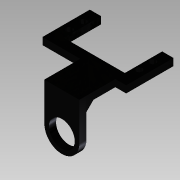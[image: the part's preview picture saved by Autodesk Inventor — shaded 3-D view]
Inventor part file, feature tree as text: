
AUTODESK INVENTOR PART (.ipt)
format: ipt  version: 2015 SP1 (Build 190203100, 203)  size: 286,208 bytes
history: native  units: mm
features: extrude x12, sketch x11, projected_geometry x4, plane x2, mirror x1
ambient origin geometry x8: Origin, YZ Plane, XZ Plane, XY Plane, X Axis, Y Axis, Z Axis, Center Point
bodies: Solid1 (feature_tree)
feature tree (30):
  sketch  "Sketch1"  dims[d19=3.0mm d20=0.0mm d22=39.4615mm]
  extrude  "Extrusion1"  Depth=39.4615mm
  plane  "Work Plane1"
  extrude  "Extrusion2"  Depth=24.75mm TaperAngle=0.0deg
  extrude  "Extrusion3"  Depth=24.75mm
  extrude  "Extrusion4"  Depth=4.980307mm
  extrude  "Extrusion5"  Depth=10.0mm TaperAngle=0.0deg
  extrude  "Extrusion6"  Depth=2.0mm
  extrude  "Extrusion7"  Depth=5.0mm TaperAngle=0.0deg
  extrude  "Extrusion8"  Depth=5.0mm TaperAngle=0.0deg
  extrude  "Extrusion9"  Depth=1.0mm
  mirror  "Mirror1"
  extrude  "Extrusion10"  TaperAngle=0.0deg  [1 undecoded]
  extrude  "Extrusion11"  Depth=5.0mm
  plane  "Work Plane2"
  sketch  "Sketch12"  dims[d64=7.0mm d65=6.460614mm d66=5.0mm d67=0.0mm d68=7.974mm d69=5.0mm d70=5.0mm d71=0.0mm d72=59.16mm d73=5.0mm d74=0.0mm d75=2.0mm d76=0.0mm d78=-9.545mm d79=5.0mm d80=45.0deg d81=24.75mm d82=0.0mm d83=5.0mm]
  extrude  "Extrusion12"  Depth=5.0mm TaperAngle=0.0deg
  sketch  "Sketch2"  dims[d23=18.25mm d24=24.75mm d25=24.75mm d26=25.0mm d27=25.0mm d32=3.0mm d33=0.0mm]
  sketch  "Sketch3"  dims[d38=90.0deg d39=24.75mm]
  projected_geometry  "Projected Loop1"
  projected_geometry  "Projected Loop2"
  sketch  "Sketch4"  dims[d41=90.0deg d42=4.980307mm d43=4.980307mm]
  projected_geometry  "Projected Loop3"
  sketch  "Sketch5"  dims[d44=4.980307mm d45=4.980307mm d46=10.0mm d47=0.0mm]
  sketch  "Sketch6"  dims[d50=2.0mm d51=0.0mm d52=2.0mm]
  sketch  "Sketch7"  dims[d53=2.0mm d54=5.0mm d55=0.0mm]
  sketch  "Sketch8"  dims[d56=1.0mm d57=5.0mm d58=0.0mm]
  sketch  "Sketch9"  dims[d59=1.0mm d60=1.0mm]
  sketch  "Sketch10"  dims[d61=0.0mm d62=0.0mm d63=0.0mm]
  projected_geometry  "Projected Loop4"
note: 1 required parameter value undecoded (feature->parameter linkage not recoverable at this tier; creation-order binding heuristic only, values carry confidence <= 0.55)
